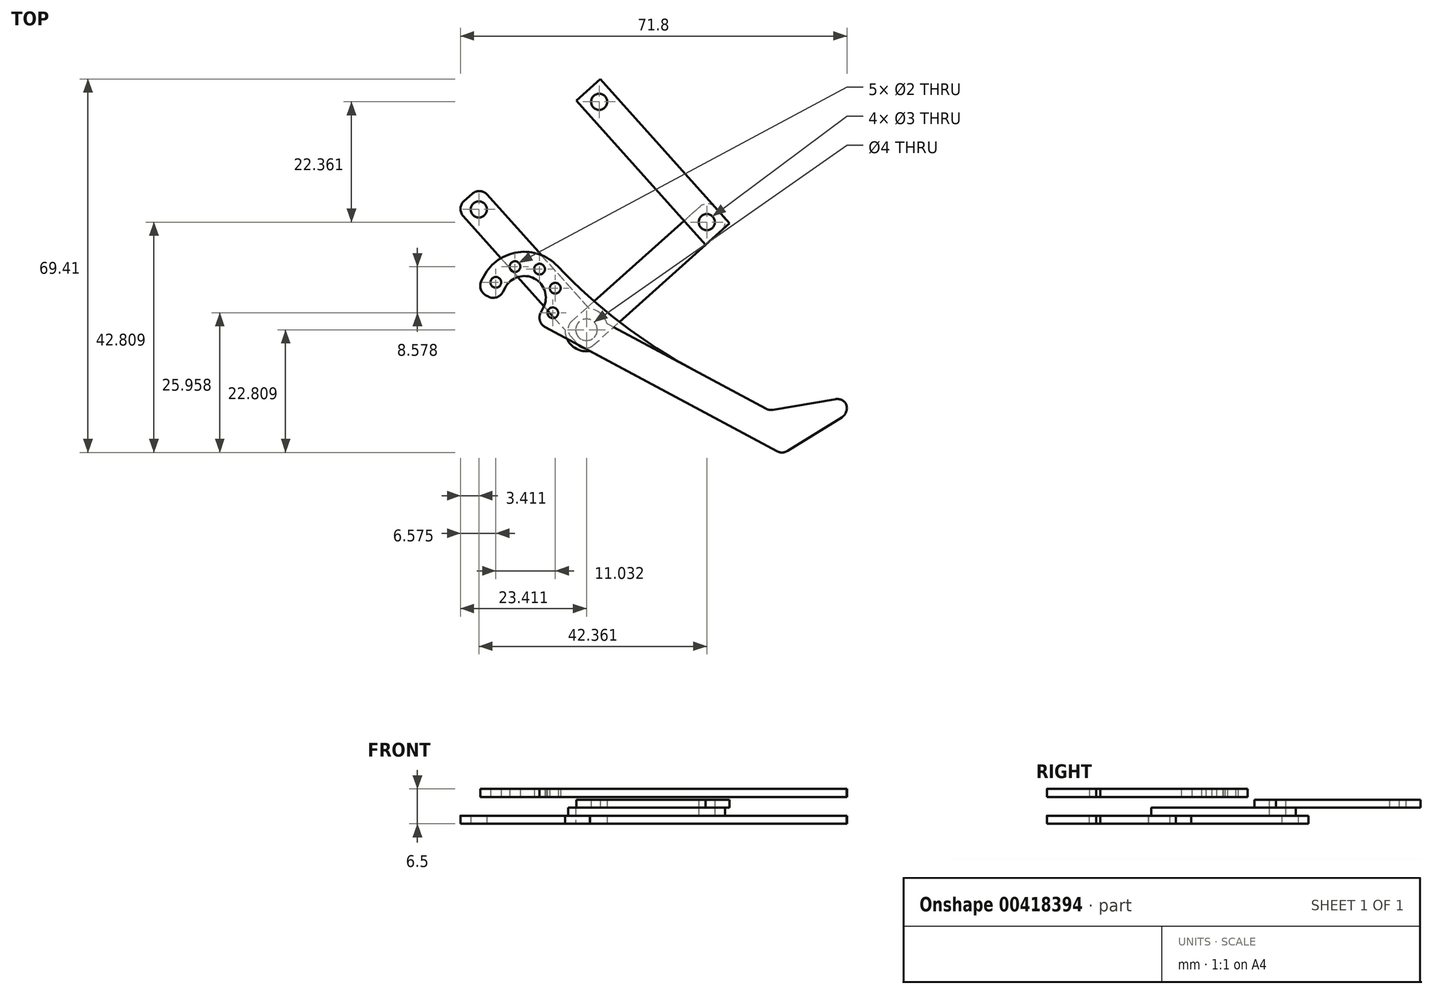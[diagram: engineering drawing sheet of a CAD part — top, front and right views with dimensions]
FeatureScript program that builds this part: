
annotation { "Feature Type Name" : "Feature", "Feature Type Description" : "" }
export const myFeature = defineFeature(function(context is Context, id is Id, definition is map)
    precondition{}
    {
        {
            var Q0;
            Q0=qCreatedBy(makeId("Top.planeOp"),FACE);
            var sketch = newSketch(context, id + "F0", { "sketchPlane" : qUnion([Q0])});
            skLineSegment(sketch, "E0", {"start": v(-22.7, 25.39) * mm, "end": v(0, 0) * mm});
            skLineSegment(sketch, "E1", {"start": v(0, 0) * mm, "end": v(29.34, -15.73) * mm});
            skLineSegment(sketch, "E2", {"start": v(37.93, -20.33) * mm, "end": v(40.76, -15.04) * mm});
            skLineSegment(sketch, "E3", {"start": v(40.76, -15.04) * mm, "end": v(3.77, 4.79) * mm});
            skLineSegment(sketch, "E4", {"start": v(3.77, 4.79) * mm, "end": v(-18.23, 29.39) * mm});
            skLineSegment(sketch, "E5", {"start": v(-18.23, 29.39) * mm, "end": v(-22.7, 25.39) * mm});
            skCircle(sketch, "E6", {"center": v(-18.47, 25.15) * mm, "radius": 1.5 * mm});
            skLineSegment(sketch, "E7", {"start": v(-20.47, 27.39) * mm, "end": v(1.53, 2.79) * mm, "construction": true});
            skLineSegment(sketch, "E8", {"start": v(1.53, 2.79) * mm, "end": v(3.77, 4.79) * mm, "construction": true});
            skLineSegment(sketch, "E9", {"start": v(1.53, 2.79) * mm, "end": v(39.34, -17.68) * mm, "construction": true});
            skCircle(sketch, "E10", {"center": v(36.7, -16.26) * mm, "radius": 1.5 * mm});
            skCircle(sketch, "E11", {"center": v(1.53, 2.79) * mm, "radius": 1.5 * mm});
            skLineSegment(sketch, "E12", {"start": v(36.7, -16.26) * mm, "end": v(15.46, -29.43) * mm, "construction": true});
            skLineSegment(sketch, "E13", {"start": v(37.93, -20.33) * mm, "end": v(17.62, -32.92) * mm});
            skLineSegment(sketch, "E14", {"start": v(17.62, -32.92) * mm, "end": v(15.46, -29.43) * mm});
            skLineSegment(sketch, "E15.MirrorCS", {"start": v(35.46, -12.2) * mm, "end": v(33.6, -13.35) * mm});
            skLineSegment(sketch, "E16.trimOffspring", {"start": v(33.75, -18.09) * mm, "end": v(37.93, -20.33) * mm});
            skLineSegment(sketch, "E17", {"start": v(29.34, -15.73) * mm, "end": v(33.75, -18.09) * mm});
            skPoint(sketch, "E18.MirrorCS.end.orphan", {"position": v(15.46, -29.43) * mm});
            skPoint(sketch, "E18.MirrorCS.start.orphan", {"position": v(13.3, -25.94) * mm});
            skLineSegment(sketch, "E19", {"start": v(29.34, -15.73) * mm, "end": v(15.46, -29.43) * mm});
            skLineSegment(sketch, "E20", {"start": v(37.93, -20.33) * mm, "end": v(50.67, -12.42) * mm});
            skLineSegment(sketch, "E21", {"start": v(50.67, -12.42) * mm, "end": v(49.1, -9.87) * mm});
            skLineSegment(sketch, "E22", {"start": v(49.1, -9.87) * mm, "end": v(35.46, -12.2) * mm});
            skSolve(sketch);
        }
        {
            var Q0;
            {var subQ1=sQuery(id+"F0.wireOp",EDGE,"E2");Q0=makeQuery(id+"F0.imprint","IMPRINT",FACE,{"disambiguationData":[TD([[makeQuery(id+"F0.imprint","IMPRINT",EDGE,{"derivedFrom":subQ1}),-1.0]])]});}
            var Q1;
            Q1=makeQuery(id+"F0.imprint","IMPRINT",FACE,{"disambiguationData":[TD([[makeQuery(id+"F0.imprint","IMPRINT",EDGE,{"derivedFrom":sQuery(id+"F0.wireOp",EDGE,"E0")}),1.0]])]});
            extrude(context, id + "F1", {"entities" : qUnion([Q0, Q1]), "depth" : 1.5 * mm});
        }
        {
            var Q0;
            Q0=makeQuery(id+"F1.opExtrude","CAP_FACE",FACE,{"disambiguationData":[OSD([sQuery(id+"F0.wireOp",EDGE,"E0"),sQuery(id+"F0.wireOp",EDGE,"E1"),sQuery(id+"F0.wireOp",EDGE,"E2"),sQuery(id+"F0.wireOp",EDGE,"E3"),sQuery(id+"F0.wireOp",EDGE,"E4"),sQuery(id+"F0.wireOp",EDGE,"E5"),sQuery(id+"F0.wireOp",EDGE,"E6"),sQuery(id+"F0.wireOp",EDGE,"E10")])],"isStart":false});
            var sketch = newSketch(context, id + "F2", { "sketchPlane" : qUnion([Q0])});
            skSolve(sketch);
        }
        {
            var Q0;
            Q0=makeQuery(id+"F2.imprint","IMPRINT",FACE,{"disambiguationData":[TD([[makeQuery(id+"F2.imprint","IMPRINT",EDGE,{"derivedFrom":makeQuery(id+"F1.opExtrude","CAP_EDGE",EDGE,{"disambiguationData":[OSD([sQuery(id+"F0.wireOp",EDGE,"E0")])],"isStart":false})}),1.0]])]});
            var sketch = newSketch(context, id + "F3", { "sketchPlane" : qUnion([Q0])});
            skLineSegment(sketch, "E23.0", {"start": v(-22.7, 25.39) * mm, "end": v(0, 0) * mm, "construction": true});
            skLineSegment(sketch, "E24.0", {"start": v(0, 0) * mm, "end": v(0, 0) * mm});
            skCircle(sketch, "E25.0", {"center": v(1.53, 2.79) * mm, "radius": 1.5 * mm});
            skLineSegment(sketch, "E26", {"start": v(1.53, 2.79) * mm, "end": v(23.9, 22.79) * mm, "construction": true});
            skCircle(sketch, "E27", {"center": v(23.9, 22.79) * mm, "radius": 1.5 * mm});
            skLineSegment(sketch, "E28", {"start": v(-2.7, 3.02) * mm, "end": v(24.13, 27.02) * mm});
            skLineSegment(sketch, "E29", {"start": v(-2.7, 3.02) * mm, "end": v(1.3, -1.45) * mm});
            skLineSegment(sketch, "E30", {"start": v(1.3, -1.45) * mm, "end": v(28.13, 22.55) * mm});
            skLineSegment(sketch, "E31", {"start": v(24.13, 27.02) * mm, "end": v(28.13, 22.55) * mm});
            skSolve(sketch);
        }
        {
            var Q0;
            Q0=qSketchRegion(id+"F3",true);
            extrude(context, id + "F4", {"entities" : qUnion([Q0]), "depth" : 1.5 * mm});
        }
        {
            var Q0;
            Q0=makeQuery(id+"F4.opExtrude","CAP_FACE",FACE,{"disambiguationData":[OSD([sQuery(id+"F3.wireOp",EDGE,"E25.0"),sQuery(id+"F3.wireOp",EDGE,"E27"),sQuery(id+"F3.wireOp",EDGE,"E28"),sQuery(id+"F3.wireOp",EDGE,"E29"),sQuery(id+"F3.wireOp",EDGE,"E30"),sQuery(id+"F3.wireOp",EDGE,"E31")])],"isStart":false});
            var sketch = newSketch(context, id + "F5", { "sketchPlane" : qUnion([Q0])});
            skLineSegment(sketch, "E32", {"start": v(28.13, 22.55) * mm, "end": v(4.13, 49.39) * mm});
            skCircle(sketch, "E33.0", {"center": v(23.9, 22.79) * mm, "radius": 1.5 * mm});
            skLineSegment(sketch, "E34", {"start": v(23.9, 22.79) * mm, "end": v(3.9, 45.15) * mm, "construction": true});
            skLineSegment(sketch, "E35", {"start": v(4.13, 49.39) * mm, "end": v(-0.34, 45.39) * mm});
            skLineSegment(sketch, "E36", {"start": v(-0.34, 45.39) * mm, "end": v(23.66, 18.55) * mm});
            skCircle(sketch, "E37", {"center": v(3.9, 45.15) * mm, "radius": 1.5 * mm});
            skLineSegment(sketch, "E38", {"start": v(23.66, 18.55) * mm, "end": v(28.13, 22.55) * mm});
            skSolve(sketch);
        }
        {
            var Q0;
            Q0=qSketchRegion(id+"F5",true);
            extrude(context, id + "F6", {"entities" : qUnion([Q0]), "depth" : 1.5 * mm});
        }
        {
            var Q0;
            Q0=makeQuery(id+"F1.opExtrude","SWEPT_EDGE",EDGE,{"disambiguationData":[OSD([sQuery(id+"F0.wireOp",EDGE,"E4"),sQuery(id+"F0.wireOp",EDGE,"E5")])]});
            var Q1;
            Q1=makeQuery(id+"F1.opExtrude","SWEPT_EDGE",EDGE,{"disambiguationData":[OSD([sQuery(id+"F0.wireOp",EDGE,"E0"),sQuery(id+"F0.wireOp",EDGE,"E5")])]});
            var Q2;
            Q2=makeQuery(id+"F4.opExtrude","SWEPT_EDGE",EDGE,{"disambiguationData":[OSD([sQuery(id+"F0.wireOp",EDGE,"E0"),sQuery(id+"F3.wireOp",EDGE,"E28"),sQuery(id+"F3.wireOp",EDGE,"E29")])]});
            var Q3;
            Q3=makeQuery(id+"F4.opExtrude","SWEPT_EDGE",EDGE,{"disambiguationData":[OSD([sQuery(id+"F3.wireOp",EDGE,"E29"),sQuery(id+"F3.wireOp",EDGE,"E30")])]});
            var Q4;
            Q4=makeQuery(id+"F4.opExtrude","SWEPT_EDGE",EDGE,{"disambiguationData":[OSD([sQuery(id+"F3.wireOp",EDGE,"E28"),sQuery(id+"F3.wireOp",EDGE,"E31")])]});
            var Q5;
            Q5=makeQuery(id+"F4.opExtrude","SWEPT_EDGE",EDGE,{"disambiguationData":[OSD([sQuery(id+"F3.wireOp",EDGE,"E30"),sQuery(id+"F3.wireOp",EDGE,"E31")])]});
            var Q6;
            Q6=makeQuery(id+"F1.opExtrude","SWEPT_EDGE",EDGE,{"disambiguationData":[OSD([sQuery(id+"F0.wireOp",EDGE,"E3"),sQuery(id+"F0.wireOp",EDGE,"E4")])]});
            var Q7;
            Q7=makeQuery(id+"F1.opExtrude","SWEPT_EDGE",EDGE,{"disambiguationData":[OSD([sQuery(id+"F0.wireOp",EDGE,"E3"),sQuery(id+"F0.wireOp",EDGE,"E22")])]});
            var Q8;
            Q8=makeQuery(id+"F1.opExtrude","SWEPT_EDGE",EDGE,{"disambiguationData":[OSD([sQuery(id+"F0.wireOp",EDGE,"E21"),sQuery(id+"F0.wireOp",EDGE,"E22")])]});
            var Q9;
            Q9=makeQuery(id+"F1.opExtrude","SWEPT_EDGE",EDGE,{"disambiguationData":[OSD([sQuery(id+"F0.wireOp",EDGE,"E20"),sQuery(id+"F0.wireOp",EDGE,"E21")])]});
            var Q10;
            Q10=makeQuery(id+"F1.opExtrude","SWEPT_EDGE",EDGE,{"disambiguationData":[OSD([sQuery(id+"F0.wireOp",EDGE,"E2"),sQuery(id+"F0.wireOp",EDGE,"E13"),sQuery(id+"F0.wireOp",EDGE,"E16.trimOffspring"),sQuery(id+"F0.wireOp",EDGE,"E20")])]});
            var Q11;
            Q11=makeQuery(id+"F1.opExtrude","SWEPT_EDGE",EDGE,{"disambiguationData":[OSD([sQuery(id+"F0.wireOp",EDGE,"E0"),sQuery(id+"F0.wireOp",EDGE,"E1")])]});
            fillet(context, id + "F7", {"entities" : qUnion([Q0, Q1, Q2, Q3, Q4, Q5, Q6, Q7, Q8, Q9, Q10, Q11]), "radius" : 2 * mm, "tangentPropagation" : true, "allowEdgeOverflow" : false});
        }
        {
            var Q0;
            Q0=makeQuery(id+"F1.opExtrude","CAP_FACE",FACE,{"disambiguationData":[OSD([sQuery(id+"F0.wireOp",EDGE,"E0"),sQuery(id+"F0.wireOp",EDGE,"E1"),sQuery(id+"F0.wireOp",EDGE,"E3"),sQuery(id+"F0.wireOp",EDGE,"E4"),sQuery(id+"F0.wireOp",EDGE,"E5"),sQuery(id+"F0.wireOp",EDGE,"E6"),sQuery(id+"F0.wireOp",EDGE,"E10"),sQuery(id+"F0.wireOp",EDGE,"E11"),sQuery(id+"F0.wireOp",EDGE,"E16.trimOffspring"),sQuery(id+"F0.wireOp",EDGE,"E17"),sQuery(id+"F0.wireOp",EDGE,"E20"),sQuery(id+"F0.wireOp",EDGE,"E21"),sQuery(id+"F0.wireOp",EDGE,"E22")])],"isStart":true});
            var sketch = newSketch(context, id + "F8", { "sketchPlane" : qUnion([Q0])});
            skCircle(sketch, "E39", {"center": v(1.53, -2.79) * mm, "radius": 4 * mm});
            skCircle(sketch, "E40", {"center": v(1.53, -2.79) * mm, "radius": 2 * mm});
            skSolve(sketch);
        }
        {
            var Q0;
            Q0=qSketchRegion(id+"F8",true);
            extrude(context, id + "F9", {"entities" : qUnion([Q0]), "operationType" : NewBodyOperationType.ADD, "oppositeDirection" : true, "depth" : 1.5 * mm});
        }
        {
            var Q0;
            Q0=makeQuery(id+"F8.imprint","IMPRINT",FACE,{"disambiguationData":[TD([[makeQuery(id+"F8.imprint","IMPRINT",EDGE,{"derivedFrom":sQuery(id+"F8.wireOp",EDGE,"E40")}),1.0]])]});
            extrude(context, id + "F10", {"entities" : qUnion([Q0]), "operationType" : NewBodyOperationType.REMOVE, "endBound" : BoundingType.UP_TO_NEXT, "oppositeDirection" : true, "depth" : 25 * mm});
        }
        {
            var Q0;
            Q0=qCreatedBy(makeId("Top.planeOp"),FACE);
            cPlane(context, id + "F11", {"entities" : qUnion([Q0]), "cplaneType" : CPlaneType.OFFSET, "offset" : 5 * mm, "width" : 150 * mm, "height" : 150 * mm});
        }
        {
            var Q0;
            Q0=qCreatedBy(id+"F11.planeOp",FACE);
            var sketch = newSketch(context, id + "F12", { "sketchPlane" : qUnion([Q0])});
            skLineSegment(sketch, "E41.0", {"start": v(34.86, -11.87) * mm, "end": v(5.36, 3.93) * mm});
            skLineSegment(sketch, "E42.0", {"start": v(2.17, -1.16) * mm, "end": v(36.9, -19.78) * mm});
            skArc(sketch, "E43.0", {"start": v(36.14, -12.08) * mm, "mid": v(35.48, -12.09) * mm, "end": v(34.86, -11.87) * mm});
            skLineSegment(sketch, "E44.0", {"start": v(47.77, -10.1) * mm, "end": v(36.14, -12.08) * mm});
            skArc(sketch, "E45.0", {"start": v(36.9, -19.78) * mm, "mid": v(37.92, -20.02) * mm, "end": v(38.9, -19.72) * mm});
            skLineSegment(sketch, "E46.0", {"start": v(38.9, -19.72) * mm, "end": v(48.97, -13.48) * mm});
            skArc(sketch, "E47.0", {"start": v(48.97, -13.48) * mm, "mid": v(49.85, -12.32) * mm, "end": v(49.7, -10.87) * mm});
            skArc(sketch, "E48.0", {"start": v(49.7, -10.87) * mm, "mid": v(48.84, -10.21) * mm, "end": v(47.77, -10.1) * mm});
            skLineSegment(sketch, "E49", {"start": v(34.86, -11.87) * mm, "end": v(32.02, -17.16) * mm, "construction": true});
            skLineSegment(sketch, "E50", {"start": v(33.44, -14.52) * mm, "end": v(-10.02, 8.77) * mm, "construction": true});
            skCircle(sketch, "E51", {"center": v(-10.02, 8.77) * mm, "radius": 4 * mm});
            skLineSegment(sketch, "E52", {"start": v(-8.13, 12.3) * mm, "end": v(-11.9, 5.25) * mm, "construction": true});
            skCircle(sketch, "E53", {"center": v(-12.85, 3.48) * mm, "radius": 1 * mm, "construction": true});
            skLineSegment(sketch, "E54", {"start": v(-11.9, 5.25) * mm, "end": v(-12.85, 3.48) * mm, "construction": true});
            skCircle(sketch, "E55.1.0", {"center": v(-8.28, 3.03) * mm, "radius": 1 * mm, "construction": true});
            skCircle(sketch, "E55.2.0", {"center": v(-4.73, 5.94) * mm, "radius": 1 * mm});
            skCircle(sketch, "E55.3.0", {"center": v(-4.27, 10.5) * mm, "radius": 1 * mm});
            skCircle(sketch, "E55.4.0", {"center": v(-7.18, 14.06) * mm, "radius": 1 * mm});
            skCircle(sketch, "E55.5.0", {"center": v(-11.75, 14.52) * mm, "radius": 1 * mm});
            skCircle(sketch, "E55.6.0", {"center": v(-15.3, 11.6) * mm, "radius": 1 * mm});
            skCircle(sketch, "E55.7.0", {"center": v(-15.76, 7.04) * mm, "radius": 1 * mm, "construction": true});
            skLineSegment(sketch, "E56", {"start": v(-6.5, 6.88) * mm, "end": v(-7.9, 4.24) * mm});
            skLineSegment(sketch, "E57", {"start": v(-7.9, 4.24) * mm, "end": v(2.17, -1.16) * mm});
            skPoint(sketch, "E58", {"position": v(-6.5, 6.88) * mm});
            skLineSegment(sketch, "E59.MirrorCS", {"start": v(-13.54, 10.66) * mm, "end": v(-14.96, 8.02) * mm});
            skLineSegment(sketch, "E60", {"start": v(-14.96, 8.02) * mm, "end": v(-18.93, 10.14) * mm});
            skLineSegment(sketch, "E61", {"start": v(-18.93, 10.14) * mm, "end": v(-17.5, 12.79) * mm});
            skLineSegment(sketch, "E62", {"start": v(-17.5, 12.79) * mm, "end": v(-13.54, 10.66) * mm, "construction": true});
            skArc(sketch, "E63", {"start": v(-1.59, 7.66) * mm, "mid": v(-7.4, 16.86) * mm, "end": v(-17.5, 12.79) * mm});
            skLineSegment(sketch, "E64", {"start": v(5.36, 3.93) * mm, "end": v(-1.59, 7.66) * mm});
            skSolve(sketch);
        }
        {
            var Q0;
            Q0=makeQuery(id+"F12.imprint","IMPRINT",FACE,{"disambiguationData":[TD([[makeQuery(id+"F12.imprint","IMPRINT",EDGE,{"derivedFrom":sQuery(id+"F12.wireOp",EDGE,"E41.0")}),1.0]])]});
            extrude(context, id + "F13", {"entities" : qUnion([Q0]), "depth" : 1.5 * mm});
        }
        {
            var Q0;
            Q0=makeQuery(id+"F13.opExtrude","SWEPT_EDGE",EDGE,{"disambiguationData":[OSD([sQuery(id+"F12.wireOp",EDGE,"E63"),sQuery(id+"F12.wireOp",EDGE,"E64")])]});
            fillet(context, id + "F14", {"entities" : qUnion([Q0]), "radius" : 100 * mm, "tangentPropagation" : true, "allowEdgeOverflow" : false});
        }
        {
            var Q0;
            Q0=makeQuery(id+"F13.opExtrude","SWEPT_EDGE",EDGE,{"disambiguationData":[OSD([sQuery(id+"F12.wireOp",EDGE,"E60"),sQuery(id+"F12.wireOp",EDGE,"E61")])]});
            var Q1;
            Q1=makeQuery(id+"F13.opExtrude","SWEPT_EDGE",EDGE,{"disambiguationData":[OSD([sQuery(id+"F12.wireOp",EDGE,"E59.MirrorCS"),sQuery(id+"F12.wireOp",EDGE,"E60")])]});
            var Q2;
            Q2=makeQuery(id+"F13.opExtrude","SWEPT_EDGE",EDGE,{"disambiguationData":[OSD([sQuery(id+"F12.wireOp",EDGE,"E56"),sQuery(id+"F12.wireOp",EDGE,"E57")])]});
            fillet(context, id + "F15", {"entities" : qUnion([Q0, Q1, Q2]), "radius" : 2 * mm, "tangentPropagation" : true, "allowEdgeOverflow" : false});
        }
        {
            var Q0;
            Q0=makeQuery(id+"F0.imprint","IMPRINT",FACE,{"disambiguationData":[TD([[makeQuery(id+"F0.imprint","IMPRINT",EDGE,{"derivedFrom":sQuery(id+"F0.wireOp",EDGE,"E10")}),1.0]])]});
            extrude(context, id + "F16", {"entities" : qUnion([Q0]), "operationType" : NewBodyOperationType.ADD, "depth" : 1.5 * mm});
        }
    });
